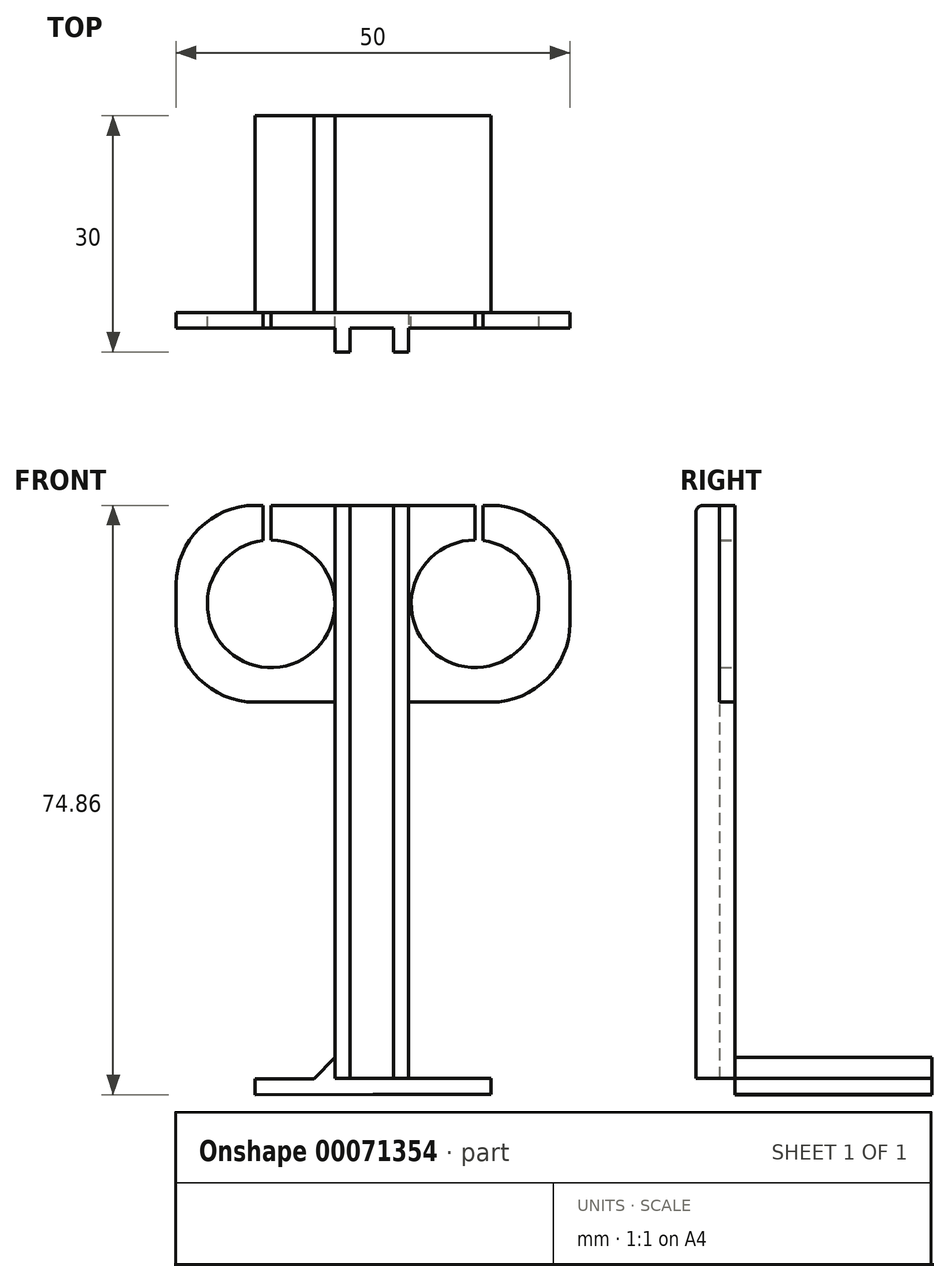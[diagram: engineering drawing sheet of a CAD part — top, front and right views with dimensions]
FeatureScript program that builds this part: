
annotation { "Feature Type Name" : "Feature", "Feature Type Description" : "" }
export const myFeature = defineFeature(function(context is Context, id is Id, definition is map)
    precondition{}
    {
        {
            var Q0;
            Q0=qCreatedBy(makeId("Front.planeOp"),FACE);
            var sketch = newSketch(context, id + "F0", { "sketchPlane" : qUnion([Q0])});
            skLineSegment(sketch, "E0.bottom", {"start": v(25, -12.5) * mm, "end": v(-25, -12.5) * mm});
            skLineSegment(sketch, "E0.top", {"start": v(25, 12.5) * mm, "end": v(-25, 12.5) * mm});
            skLineSegment(sketch, "E0.left", {"start": v(25, -12.5) * mm, "end": v(25, 12.5) * mm});
            skLineSegment(sketch, "E0.right", {"start": v(-25, -12.5) * mm, "end": v(-25, 12.5) * mm});
            skPoint(sketch, "E0.middle", {"position": v(0, 0) * mm});
            skLineSegment(sketch, "E1", {"start": v(0, -12.5) * mm, "end": v(0, 12.5) * mm, "construction": true});
            skCircle(sketch, "E2", {"center": v(-12.95, 0) * mm, "radius": 8.1 * mm});
            skCircle(sketch, "E3.MirrorC", {"center": v(12.95, 0) * mm, "radius": 8.1 * mm});
            skLineSegment(sketch, "E4", {"start": v(-12.95, 8.1) * mm, "end": v(-12.95, 12.5) * mm});
            skLineSegment(sketch, "E5", {"start": v(-12.95, 12.5) * mm, "end": v(-13.95, 12.5) * mm});
            skLineSegment(sketch, "E6", {"start": v(-13.95, 12.5) * mm, "end": v(-13.95, 8.04) * mm});
            skLineSegment(sketch, "E7.MirrorCS", {"start": v(12.95, 8.1) * mm, "end": v(12.95, 12.5) * mm});
            skLineSegment(sketch, "E8.MirrorCS", {"start": v(13.95, 12.5) * mm, "end": v(13.95, 8.04) * mm});
            skLineSegment(sketch, "E9", {"start": v(-4.85, 0) * mm, "end": v(-4.85, 12.5) * mm});
            skLineSegment(sketch, "E10", {"start": v(-4.85, 12.5) * mm, "end": v(-4.85, -12.5) * mm});
            skLineSegment(sketch, "E11", {"start": v(4.5, 0) * mm, "end": v(4.5, 12.5) * mm});
            skLineSegment(sketch, "E12", {"start": v(4.49, 12.5) * mm, "end": v(4.5, -12.5) * mm});
            skLineSegment(sketch, "E13", {"start": v(-2.95, -12.5) * mm, "end": v(-2.95, 12.5) * mm});
            skLineSegment(sketch, "E14", {"start": v(2.6, -12.5) * mm, "end": v(2.6, 12.5) * mm});
            skSolve(sketch);
        }
        {
            var Q0;
            {var subQ0=sQuery(id+"F0.wireOp",EDGE,"E0.left");Q0=makeQuery(id+"F0.imprint","IMPRINT",FACE,{"disambiguationData":[TD([[makeQuery(id+"F0.imprint","IMPRINT",EDGE,{"derivedFrom":subQ0}),1.0]])]});}
            var Q1;
            {var subQ0=sQuery(id+"F0.wireOp",EDGE,"E4");Q1=makeQuery(id+"F0.imprint","IMPRINT",FACE,{"disambiguationData":[TD([[makeQuery(id+"F0.imprint","IMPRINT",EDGE,{"derivedFrom":subQ0}),-1.0]])]});}
            var Q2;
            {var subQ4=sQuery(id+"F0.wireOp",EDGE,"E0.right");Q2=makeQuery(id+"F0.imprint","IMPRINT",FACE,{"disambiguationData":[TD([[makeQuery(id+"F0.imprint","IMPRINT",EDGE,{"derivedFrom":subQ4}),-1.0]])]});}
            var Q3;
            {var subQ6=sQuery(id+"F0.wireOp",EDGE,"E13");Q3=makeQuery(id+"F0.imprint","IMPRINT",FACE,{"disambiguationData":[TD([[makeQuery(id+"F0.imprint","IMPRINT",EDGE,{"derivedFrom":subQ6}),1.0]])]});}
            var Q4;
            {var subQ0=sQuery(id+"F0.wireOp",EDGE,"E13");Q4=makeQuery(id+"F0.imprint","IMPRINT",FACE,{"disambiguationData":[TD([[makeQuery(id+"F0.imprint","IMPRINT",EDGE,{"derivedFrom":subQ0}),-1.0]])]});}
            var Q5;
            {var subQ6=sQuery(id+"F0.wireOp",EDGE,"E14");Q5=makeQuery(id+"F0.imprint","IMPRINT",FACE,{"disambiguationData":[TD([[makeQuery(id+"F0.imprint","IMPRINT",EDGE,{"derivedFrom":subQ6}),-1.0]])]});}
            extrude(context, id + "F1", {"entities" : qUnion([Q0, Q1, Q2, Q3, Q4, Q5]), "depth" : 2 * mm});
        }
        {
            var Q0;
            Q0=makeQuery(id+"F1.opExtrude","SWEPT_EDGE",EDGE,{"disambiguationData":[OSD([sQuery(id+"F0.wireOp",EDGE,"E0.bottom"),sQuery(id+"F0.wireOp",EDGE,"E0.left")])]});
            var Q1;
            Q1=makeQuery(id+"F1.opExtrude","SWEPT_EDGE",EDGE,{"disambiguationData":[OSD([sQuery(id+"F0.wireOp",EDGE,"E0.top"),sQuery(id+"F0.wireOp",EDGE,"E0.left")])]});
            var Q2;
            Q2=makeQuery(id+"F1.opExtrude","SWEPT_EDGE",EDGE,{"disambiguationData":[OSD([sQuery(id+"F0.wireOp",EDGE,"E0.top"),sQuery(id+"F0.wireOp",EDGE,"E0.right")])]});
            var Q3;
            Q3=makeQuery(id+"F1.opExtrude","SWEPT_EDGE",EDGE,{"disambiguationData":[OSD([sQuery(id+"F0.wireOp",EDGE,"E0.bottom"),sQuery(id+"F0.wireOp",EDGE,"E0.right")])]});
            fillet(context, id + "F2", {"entities" : qUnion([Q0, Q1, Q2, Q3]), "radius" : 10 * mm, "tangentPropagation" : true, "allowEdgeOverflow" : false});
        }
        {
            var Q0;
            {var subQ6=sQuery(id+"F0.wireOp",EDGE,"E14");Q0=makeQuery(id+"F0.imprint","IMPRINT",FACE,{"disambiguationData":[TD([[makeQuery(id+"F0.imprint","IMPRINT",EDGE,{"derivedFrom":subQ6}),-1.0]])]});}
            var Q1;
            {var subQ6=sQuery(id+"F0.wireOp",EDGE,"E13");Q1=makeQuery(id+"F0.imprint","IMPRINT",FACE,{"disambiguationData":[TD([[makeQuery(id+"F0.imprint","IMPRINT",EDGE,{"derivedFrom":subQ6}),1.0]])]});}
            extrude(context, id + "F3", {"entities" : qUnion([Q0, Q1]), "operationType" : NewBodyOperationType.ADD, "depth" : 5 * mm});
        }
        {
            var Q0;
            {var subQ0=sQuery(id+"F0.wireOp",EDGE,"E0.bottom");Q0=makeQuery(id+"F3.boolean.opBoolean","MERGE",FACE,{"derivedFrom":[makeQuery(id+"F1.opExtrude","SWEPT_FACE",FACE,{"disambiguationData":[OSD([subQ0])]}),makeQuery(id+"F3.opExtrude","SWEPT_FACE",FACE,{"disambiguationData":[OSD([subQ0]),TDD([makeQuery(id+"F0.imprint","IMPRINT",EDGE,{"disambiguationData":[TD([[makeQuery(id+"F0.imprint","INTERSECT",VERTEX,{"derivedFrom":[subQ0,sQuery(id+"F0.wireOp",EDGE,"E12")]}),-1.0]])],"derivedFrom":subQ0})])]}),makeQuery(id+"F3.opExtrude","SWEPT_FACE",FACE,{"disambiguationData":[OSD([subQ0]),TDD([makeQuery(id+"F0.imprint","IMPRINT",EDGE,{"disambiguationData":[TD([[makeQuery(id+"F0.imprint","INTERSECT",VERTEX,{"derivedFrom":[subQ0,sQuery(id+"F0.wireOp",EDGE,"E10")]}),1.0]])],"derivedFrom":subQ0})])]})]});}
            var sketch = newSketch(context, id + "F4", { "sketchPlane" : qUnion([Q0])});
            skLineSegment(sketch, "E15", {"start": v(-4.85, 5) * mm, "end": v(-4.85, 0) * mm});
            skLineSegment(sketch, "E16", {"start": v(-4.85, 0) * mm, "end": v(4.5, 0) * mm});
            skLineSegment(sketch, "E17", {"start": v(4.5, 0) * mm, "end": v(4.5, 2) * mm});
            skLineSegment(sketch, "E18", {"start": v(4.5, 2) * mm, "end": v(4.5, 5) * mm});
            skLineSegment(sketch, "E19", {"start": v(4.5, 5) * mm, "end": v(2.6, 5) * mm});
            skLineSegment(sketch, "E20", {"start": v(2.6, 5) * mm, "end": v(2.6, 2) * mm});
            skLineSegment(sketch, "E21", {"start": v(2.6, 2) * mm, "end": v(-2.95, 2) * mm});
            skLineSegment(sketch, "E22", {"start": v(-2.95, 2) * mm, "end": v(-2.95, 5) * mm});
            skLineSegment(sketch, "E23", {"start": v(-2.95, 5) * mm, "end": v(-4.85, 5) * mm});
            skSolve(sketch);
        }
        {
            var Q0;
            Q0 = qSketchRegion(id + "F4", true);
            extrude(context, id + "F5", {"entities" : qUnion([Q0]), "operationType" : NewBodyOperationType.ADD, "depth" : 47.8 * mm});
        }
        {
            var Q0;
            {var subQ0=sQuery(id+"F0.wireOp",EDGE,"E0.top");Q0=makeQuery(id+"F3.opExtrude","CAP_EDGE",EDGE,{"disambiguationData":[OSD([subQ0]),TDD([makeQuery(id+"F0.imprint","IMPRINT",EDGE,{"disambiguationData":[TD([[makeQuery(id+"F0.imprint","INTERSECT",VERTEX,{"derivedFrom":[subQ0,sQuery(id+"F0.wireOp",EDGE,"E10")]}),1.0]])],"derivedFrom":subQ0})])],"isStart":false});}
            var Q1;
            {var subQ0=sQuery(id+"F0.wireOp",EDGE,"E0.top");Q1=makeQuery(id+"F3.opExtrude","CAP_EDGE",EDGE,{"disambiguationData":[OSD([subQ0]),TDD([makeQuery(id+"F0.imprint","IMPRINT",EDGE,{"disambiguationData":[TD([[makeQuery(id+"F0.imprint","INTERSECT",VERTEX,{"derivedFrom":[subQ0,sQuery(id+"F0.wireOp",EDGE,"E12")]}),-1.0]])],"derivedFrom":subQ0})])],"isStart":false});}
            fillet(context, id + "F6", {"entities" : qUnion([Q0, Q1]), "radius" : 1 * mm, "tangentPropagation" : true, "allowEdgeOverflow" : false});
        }
        {
            var Q0;
            Q0=makeQuery(id+"F5.boolean.opBoolean","MERGE",FACE,{"derivedFrom":[makeQuery(id+"F1.opExtrude","CAP_FACE",FACE,{"disambiguationData":[OSD([sQuery(id+"F0.wireOp",EDGE,"E0.bottom"),sQuery(id+"F0.wireOp",EDGE,"E0.top"),sQuery(id+"F0.wireOp",EDGE,"E0.left"),sQuery(id+"F0.wireOp",EDGE,"E0.right"),sQuery(id+"F0.wireOp",EDGE,"E2"),sQuery(id+"F0.wireOp",EDGE,"E3.MirrorC"),sQuery(id+"F0.wireOp",EDGE,"E4"),sQuery(id+"F0.wireOp",EDGE,"E6"),sQuery(id+"F0.wireOp",EDGE,"E7.MirrorCS"),sQuery(id+"F0.wireOp",EDGE,"E8.MirrorCS")])],"isStart":true}),makeQuery(id+"F5.opExtrude","SWEPT_FACE",FACE,{"disambiguationData":[OSD([sQuery(id+"F4.wireOp",EDGE,"E16")])]})]});
            var sketch = newSketch(context, id + "F7", { "sketchPlane" : qUnion([Q0])});
            skLineSegment(sketch, "E24", {"start": v(-4.5, -60.3) * mm, "end": v(-15, -60.3) * mm});
            skLineSegment(sketch, "E25", {"start": v(0, -62.3) * mm, "end": v(0.18, 12.5) * mm, "construction": true});
            skPoint(sketch, "E25.endSnap0", {"position": v(0.18, -60.3) * mm});
            skLineSegment(sketch, "E26", {"start": v(-15, -60.3) * mm, "end": v(-15, -62.3) * mm});
            skLineSegment(sketch, "E27", {"start": v(-15, -62.3) * mm, "end": v(0, -62.3) * mm});
            skLineSegment(sketch, "E28.MirrorCS", {"start": v(15, -62.36) * mm, "end": v(0, -62.29) * mm});
            skLineSegment(sketch, "E29.MirrorCS", {"start": v(4.5, -60.31) * mm, "end": v(15, -60.36) * mm});
            skLineSegment(sketch, "E30.MirrorCS", {"start": v(15, -60.36) * mm, "end": v(15, -62.36) * mm});
            skLineSegment(sketch, "E31", {"start": v(-4.5, -60.3) * mm, "end": v(4.85, -60.3) * mm});
            skLineSegment(sketch, "E32", {"start": v(7.46, -60.33) * mm, "end": v(4.85, -57.61) * mm});
            skLineSegment(sketch, "E33", {"start": v(-6.55, -60.3) * mm, "end": v(-4.5, -57.71) * mm});
            skSolve(sketch);
        }
        {
            var Q0;
            Q0 = qSketchRegion(id + "F7", true);
            var Q1;
            {var subQ0=sQuery(id+"F7.wireOp",EDGE,"E26");Q1=makeQuery(id+"F7.imprint","IMPRINT",FACE,{"disambiguationData":[TD([[makeQuery(id+"F7.imprint","IMPRINT",EDGE,{"derivedFrom":subQ0}),1.0]])]});}
            var Q2;
            {var subQ0=sQuery(id+"F7.wireOp",EDGE,"E26");Q2=makeQuery(id+"F7.imprint","IMPRINT",FACE,{"disambiguationData":[TD([[makeQuery(id+"F7.imprint","IMPRINT",EDGE,{"derivedFrom":subQ0}),1.0]])]});}
            extrude(context, id + "F8", {"entities" : qUnion([Q0, Q1, Q2]), "operationType" : NewBodyOperationType.ADD, "depth" : 25 * mm});
        }
    });
